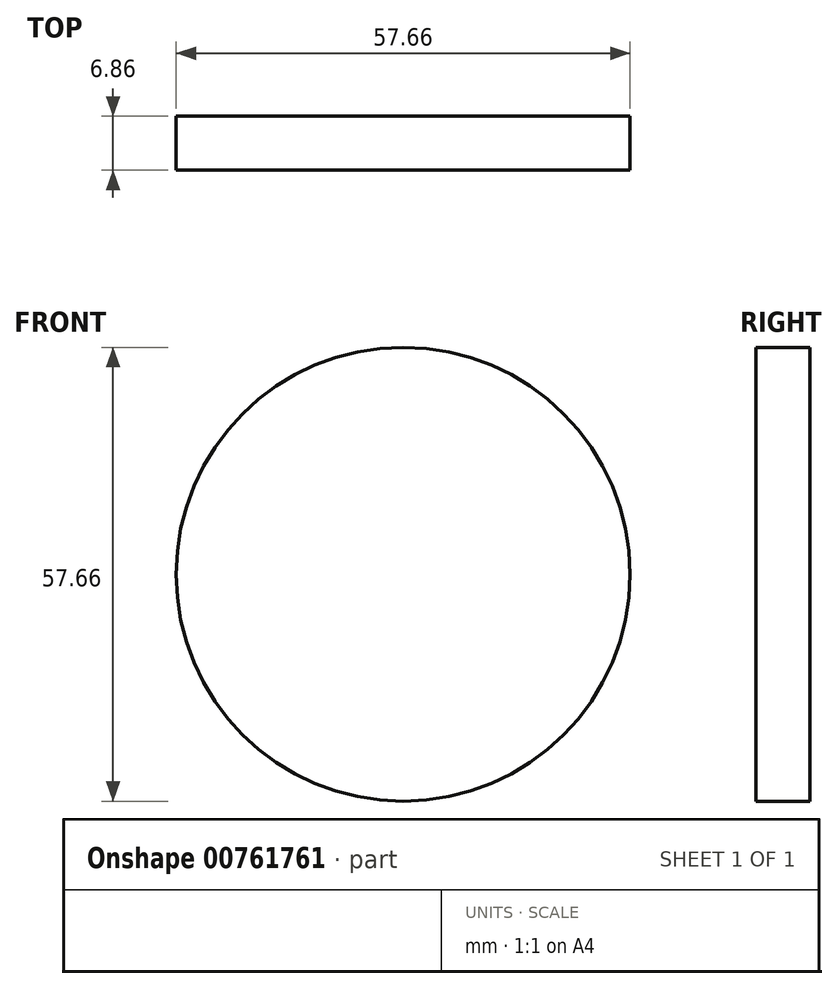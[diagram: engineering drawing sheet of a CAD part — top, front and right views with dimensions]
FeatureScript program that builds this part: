
annotation { "Feature Type Name" : "Feature", "Feature Type Description" : "" }
export const myFeature = defineFeature(function(context is Context, id is Id, definition is map)
    precondition{}
    {
        {
            var Q0;
            Q0=qCreatedBy(makeId("Front.planeOp"),FACE);
            var sketch = newSketch(context, id + "F0", { "sketchPlane" : qUnion([Q0])});
            skCircle(sketch, "E0", {"center": v(0, 35.39) * mm, "radius": 28.83 * mm});
            skSolve(sketch);
        }
        {
            var Q0;
            Q0 = qSketchRegion(id + "F0", true);
            extrude(context, id + "F1", {"entities" : qUnion([Q0]), "depth" : 6.86 * mm, "offsetDistance" : 25.4 * mm});
        }
    });
